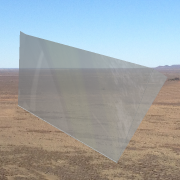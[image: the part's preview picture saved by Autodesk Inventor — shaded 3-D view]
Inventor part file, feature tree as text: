
AUTODESK INVENTOR PART (.ipt)
format: ipt  version: 2013 SP2 (Build 170200200, 200)  size: 205,824 bytes
history: native  units: in
note: dims shown in document units (in); Inventor stores cm internally (conversion verified against a paired STEP export)
features: extrude x5, sketch x5, plane x2, other x2, loft x1
ambient origin geometry x8: Origin, YZ Plane, XZ Plane, XY Plane, X Axis, Y Axis, Z Axis, Center Point
bodies: Solid1 (feature_tree)
feature tree (15):
  extrude  "Extrusion1"  Depth=1.0in
  plane  "Work Plane1"
  extrude  "Extrusion2"  Depth=0.0481in
  extrude  "Extrusion3"  Depth=0.25in
  plane  "Work Plane3"
  extrude  "Extrusion5"  Depth=7.0in
  extrude  "Extrusion6"  TaperAngle=60.0deg  [1 undecoded]
  loft  "Loft1"
  sketch  "Sketch1"  dims[d0=136.0in d1=1.0in]
  sketch  "Sketch2"  dims[d2=0.25in d3=0.0in d4=0.0481in]
  sketch  "Sketch3"  dims[d5=1.0in d6=0.25in]
  sketch  "Sketch5"  dims[d7=80.0in d8=0.0in d10=7.0in]
  sketch  "Sketch6"  dims[d11=0.25in d12=0.0in d17=60.0deg d18=1.0in d19=100.0in d20=0.25in d21=0.0in d22=20.0in d23=0.25in d24=0.0in d25=0.0in d26=90.0deg d27=0.0in d28=90.0deg]
  other  "Edges1"
  other  "Edges2"
note: 1 required parameter value undecoded (feature->parameter linkage not recoverable at this tier; creation-order binding heuristic only, values carry confidence <= 0.55)
